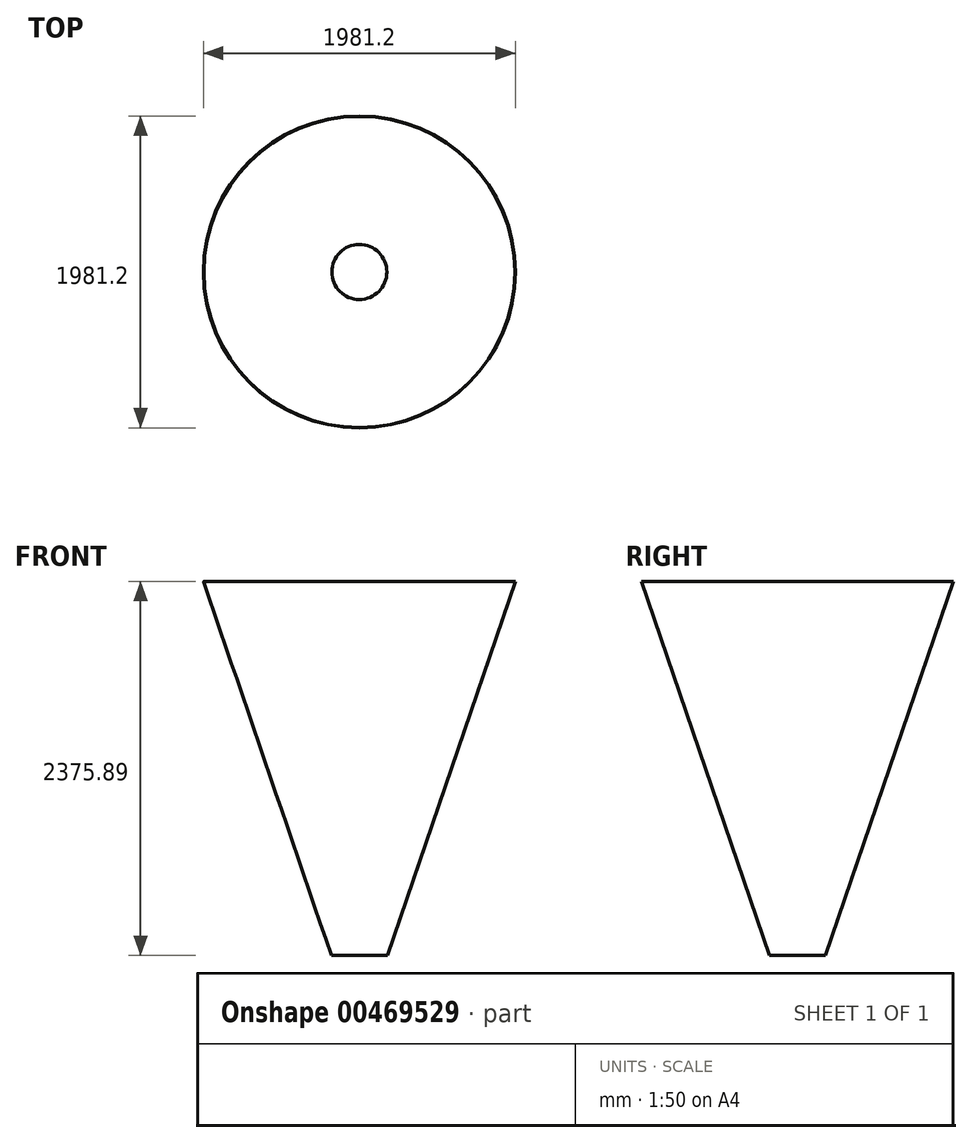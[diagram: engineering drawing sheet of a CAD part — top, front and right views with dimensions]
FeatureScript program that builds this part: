
annotation { "Feature Type Name" : "Feature", "Feature Type Description" : "" }
export const myFeature = defineFeature(function(context is Context, id is Id, definition is map)
    precondition{}
    {
        {
            var Q0;
            Q0=qCreatedBy(makeId("Front.planeOp"),FACE);
            var sketch = newSketch(context, id + "F0", { "sketchPlane" : qUnion([Q0])});
            skLineSegment(sketch, "E0", {"start": v(-177.8, 0) * mm, "end": v(-990.6, 2374.9) * mm});
            skLineSegment(sketch, "E1", {"start": v(-990.6, 2374.9) * mm, "end": v(-987.72, 2375.89) * mm});
            skLineSegment(sketch, "E2", {"start": v(-987.72, 2375.89) * mm, "end": v(-174.92, 0.99) * mm});
            skLineSegment(sketch, "E3", {"start": v(-174.92, 0.99) * mm, "end": v(-177.8, 0) * mm});
            skLineSegment(sketch, "E4", {"start": v(0, 0) * mm, "end": v(0, 2375.89) * mm, "construction": true});
            skSolve(sketch);
        }
        {
            var Q0;
            Q0 = qSketchRegion(id + "F0", true);
            var Q1;
            Q1=sQuery(id+"F0.wireOp",EDGE,"E4");
            revolve(context, id + "F1", {"surfaceOperationType" : NewSurfaceOperationType.NEW, "entities" : qUnion([Q0]), "axis" : qUnion([Q1]), "revolveType" : RevolveType.FULL});
        }
    });
